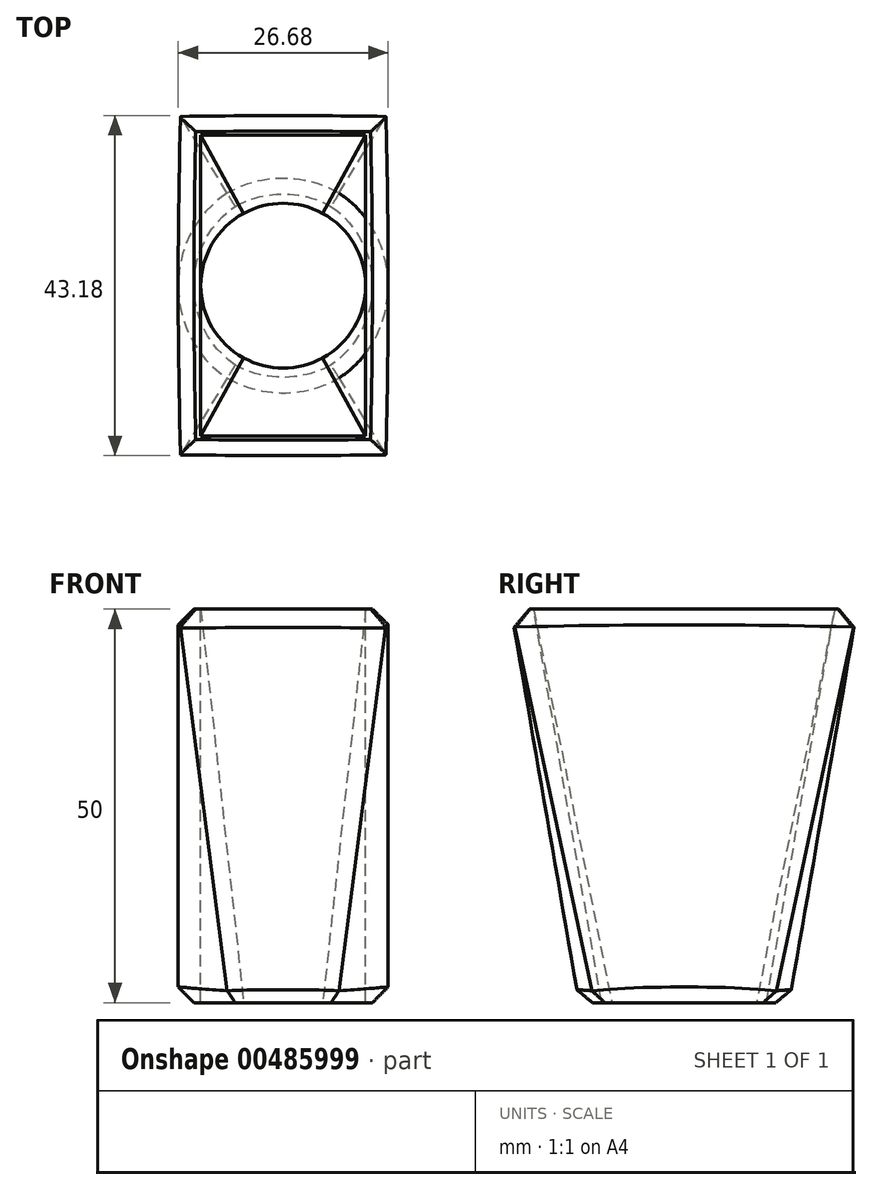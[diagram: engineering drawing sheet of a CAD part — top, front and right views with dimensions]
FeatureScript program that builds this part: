
annotation { "Feature Type Name" : "Feature", "Feature Type Description" : "" }
export const myFeature = defineFeature(function(context is Context, id is Id, definition is map)
    precondition{}
    {
        {
            var Q0;
            Q0=qCreatedBy(makeId("Top.planeOp"),FACE);
            var sketch = newSketch(context, id + "F0", { "sketchPlane" : qUnion([Q0])});
            skPoint(sketch, "E0.middle", {"position": v(0, 0) * mm});
            skArc(sketch, "E1", {"start": v(6.91, -11.4) * mm, "mid": v(13.34, 0) * mm, "end": v(6.91, 11.4) * mm});
            skArc(sketch, "E2", {"start": v(-6.91, -11.4) * mm, "mid": v(0, -13.34) * mm, "end": v(6.91, -11.4) * mm});
            skArc(sketch, "E3", {"start": v(-6.91, 11.4) * mm, "mid": v(-13.33, 0) * mm, "end": v(-6.91, -11.4) * mm});
            skArc(sketch, "E4", {"start": v(6.91, 11.4) * mm, "mid": v(0, 13.34) * mm, "end": v(-6.91, 11.4) * mm});
            skPoint(sketch, "E0.top.end.orphan", {"position": v(-13.34, -22) * mm});
            skPoint(sketch, "E0.top.start.orphan", {"position": v(13.33, -22) * mm});
            skPoint(sketch, "E0.bottom.start.orphan", {"position": v(13.34, 22) * mm});
            skPoint(sketch, "E0.right.start.orphan", {"position": v(-13.33, 22) * mm});
            skSolve(sketch);
        }
        {
            var Q0;
            Q0=qCreatedBy(makeId("Top.planeOp"),FACE);
            cPlane(context, id + "F1", {"entities" : qUnion([Q0]), "cplaneType" : CPlaneType.OFFSET, "offset" : 50 * mm, "width" : 150 * mm, "height" : 150 * mm});
        }
        {
            var Q0;
            Q0=qCreatedBy(id+"F1.planeOp",FACE);
            var sketch = newSketch(context, id + "F2", { "sketchPlane" : qUnion([Q0])});
            skLineSegment(sketch, "E5.bottom", {"start": v(13.33, -22) * mm, "end": v(-13.34, -22) * mm});
            skLineSegment(sketch, "E5.top", {"start": v(13.34, 22) * mm, "end": v(-13.33, 22) * mm});
            skLineSegment(sketch, "E5.left", {"start": v(13.33, -22) * mm, "end": v(13.34, 22) * mm});
            skLineSegment(sketch, "E5.right", {"start": v(-13.34, -22) * mm, "end": v(-13.33, 22) * mm});
            skPoint(sketch, "E5.middle", {"position": v(0, 0) * mm});
            skSolve(sketch);
        }
        {
            var Q0;
            Q0=makeQuery(id+"F0.imprint","IMPRINT",FACE,{"disambiguationData":[TD([[makeQuery(id+"F0.imprint","IMPRINT",EDGE,{"derivedFrom":sQuery(id+"F0.wireOp",EDGE,"E1")}),1.0]])]});
            var Q1;
            Q1=makeQuery(id+"F2.imprint","IMPRINT",FACE,{"disambiguationData":[TD([[makeQuery(id+"F2.imprint","IMPRINT",EDGE,{"derivedFrom":sQuery(id+"F2.wireOp",EDGE,"E5.bottom")}),-1.0]])]});
            loft(context, id + "F3", {"sheetProfilesArray" : [{ "sheetProfileEntities" : qUnion([Q0]) }, { "sheetProfileEntities" : qUnion([Q1]) }]});
        }
        {
            var Q0;
            Q0=makeQuery(id+"F3.opLoft","CAP_FACE",FACE,{"disambiguationData":[OSD([makeQuery(id+"F0.imprint","IMPRINT",FACE,{"disambiguationData":[TD([[makeQuery(id+"F0.imprint","IMPRINT",EDGE,{"derivedFrom":sQuery(id+"F0.wireOp",EDGE,"E1")}),1.0]])]})])],"isStart":true});
            var sketch = newSketch(context, id + "F4", { "sketchPlane" : qUnion([Q0])});
            skPoint(sketch, "E6.middle", {"position": v(0, 0) * mm});
            skArc(sketch, "E7", {"start": v(-5.02, -9.18) * mm, "mid": v(0, -10.47) * mm, "end": v(5.02, -9.18) * mm});
            skArc(sketch, "E8", {"start": v(-5.02, 9.18) * mm, "mid": v(-10.47, 0) * mm, "end": v(-5.02, -9.18) * mm});
            skArc(sketch, "E9", {"start": v(5.02, 9.18) * mm, "mid": v(0, 10.47) * mm, "end": v(-5.02, 9.18) * mm});
            skArc(sketch, "E10", {"start": v(5.02, -9.18) * mm, "mid": v(10.47, 0) * mm, "end": v(5.02, 9.18) * mm});
            skPoint(sketch, "E11.orphan", {"position": v(-10.47, -19.13) * mm});
            skPoint(sketch, "E6.bottom.start.orphan", {"position": v(-10.46, 19.13) * mm});
            skPoint(sketch, "E6.right.start.orphan", {"position": v(10.47, 19.13) * mm});
            skPoint(sketch, "E12.orphan", {"position": v(10.46, -19.13) * mm});
            skSolve(sketch);
        }
        {
            var Q0;
            Q0=makeQuery(id+"F3.opLoft","CAP_FACE",FACE,{"disambiguationData":[OSD([makeQuery(id+"F2.imprint","IMPRINT",FACE,{"disambiguationData":[TD([[makeQuery(id+"F2.imprint","IMPRINT",EDGE,{"derivedFrom":sQuery(id+"F2.wireOp",EDGE,"E5.bottom")}),-1.0]])]})])],"isStart":true});
            var sketch = newSketch(context, id + "F5", { "sketchPlane" : qUnion([Q0])});
            skLineSegment(sketch, "E13.bottom", {"start": v(10.46, -19.13) * mm, "end": v(-10.47, -19.13) * mm});
            skLineSegment(sketch, "E13.top", {"start": v(10.47, 19.13) * mm, "end": v(-10.46, 19.13) * mm});
            skLineSegment(sketch, "E13.left", {"start": v(10.46, -19.13) * mm, "end": v(10.47, 19.13) * mm});
            skLineSegment(sketch, "E13.right", {"start": v(-10.47, -19.13) * mm, "end": v(-10.46, 19.13) * mm});
            skPoint(sketch, "E13.middle", {"position": v(0, 0) * mm});
            skSolve(sketch);
        }
        {
            var Q1;
            Q1=makeQuery(id+"F5.imprint","IMPRINT",FACE,{"disambiguationData":[TD([[makeQuery(id+"F5.imprint","IMPRINT",EDGE,{"derivedFrom":sQuery(id+"F5.wireOp",EDGE,"E13.bottom")}),-1.0]])]});
            var Q2;
            Q2=makeQuery(id+"F4.imprint","IMPRINT",FACE,{"disambiguationData":[TD([[makeQuery(id+"F4.imprint","IMPRINT",EDGE,{"derivedFrom":sQuery(id+"F4.wireOp",EDGE,"E7")}),1.0]])]});
            loft(context, id + "F6", {"operationType" : NewBodyOperationType.REMOVE, "sheetProfilesArray" : [{ "sheetProfileEntities" : qUnion([Q1]) }, { "sheetProfileEntities" : qUnion([Q2]) }]});
        }
        {
            var Q0;
            Q0=makeQuery(id+"F3.opLoft","MID_CAP_EDGE",EDGE,{"disambiguationData":[OSD([sQuery(id+"F0.wireOp",EDGE,"E1"),sQuery(id+"F0.wireOp",EDGE,"E3"),sQuery(id+"F0.wireOp",EDGE,"E4")])],"capPos":0.0});
            var Q1;
            Q1=makeQuery(id+"F3.opLoft","MID_CAP_EDGE",EDGE,{"disambiguationData":[OSD([sQuery(id+"F0.wireOp",EDGE,"E2"),sQuery(id+"F0.wireOp",EDGE,"E3"),sQuery(id+"F0.wireOp",EDGE,"E4")])],"capPos":0.0});
            var Q2;
            Q2=makeQuery(id+"F3.opLoft","MID_CAP_EDGE",EDGE,{"disambiguationData":[OSD([sQuery(id+"F0.wireOp",EDGE,"E1"),sQuery(id+"F0.wireOp",EDGE,"E2"),sQuery(id+"F0.wireOp",EDGE,"E3")])],"capPos":0.0});
            var Q3;
            Q3=makeQuery(id+"F3.opLoft","MID_CAP_EDGE",EDGE,{"disambiguationData":[OSD([sQuery(id+"F0.wireOp",EDGE,"E1"),sQuery(id+"F0.wireOp",EDGE,"E2"),sQuery(id+"F0.wireOp",EDGE,"E4")])],"capPos":0.0});
            var Q4;
            Q4=makeQuery(id+"F3.opLoft","MID_CAP_EDGE",EDGE,{"disambiguationData":[OSD([sQuery(id+"F2.wireOp",EDGE,"E5.bottom"),sQuery(id+"F2.wireOp",EDGE,"E5.top"),sQuery(id+"F2.wireOp",EDGE,"E5.left")])],"capPos":1.0});
            var Q5;
            Q5=makeQuery(id+"F3.opLoft","MID_CAP_EDGE",EDGE,{"disambiguationData":[OSD([sQuery(id+"F2.wireOp",EDGE,"E5.top"),sQuery(id+"F2.wireOp",EDGE,"E5.left"),sQuery(id+"F2.wireOp",EDGE,"E5.right")])],"capPos":1.0});
            var Q6;
            Q6=makeQuery(id+"F3.opLoft","MID_CAP_EDGE",EDGE,{"disambiguationData":[OSD([sQuery(id+"F2.wireOp",EDGE,"E5.bottom"),sQuery(id+"F2.wireOp",EDGE,"E5.top"),sQuery(id+"F2.wireOp",EDGE,"E5.right")])],"capPos":1.0});
            var Q7;
            Q7=makeQuery(id+"F3.opLoft","MID_CAP_EDGE",EDGE,{"disambiguationData":[OSD([sQuery(id+"F2.wireOp",EDGE,"E5.bottom"),sQuery(id+"F2.wireOp",EDGE,"E5.left"),sQuery(id+"F2.wireOp",EDGE,"E5.right")])],"capPos":1.0});
            chamfer(context, id + "F7", {"entities" : qUnion([Q0, Q1, Q2, Q3, Q4, Q5, Q6, Q7]), "width" : 2 * mm, "tangentPropagation" : true});
        }
    });
